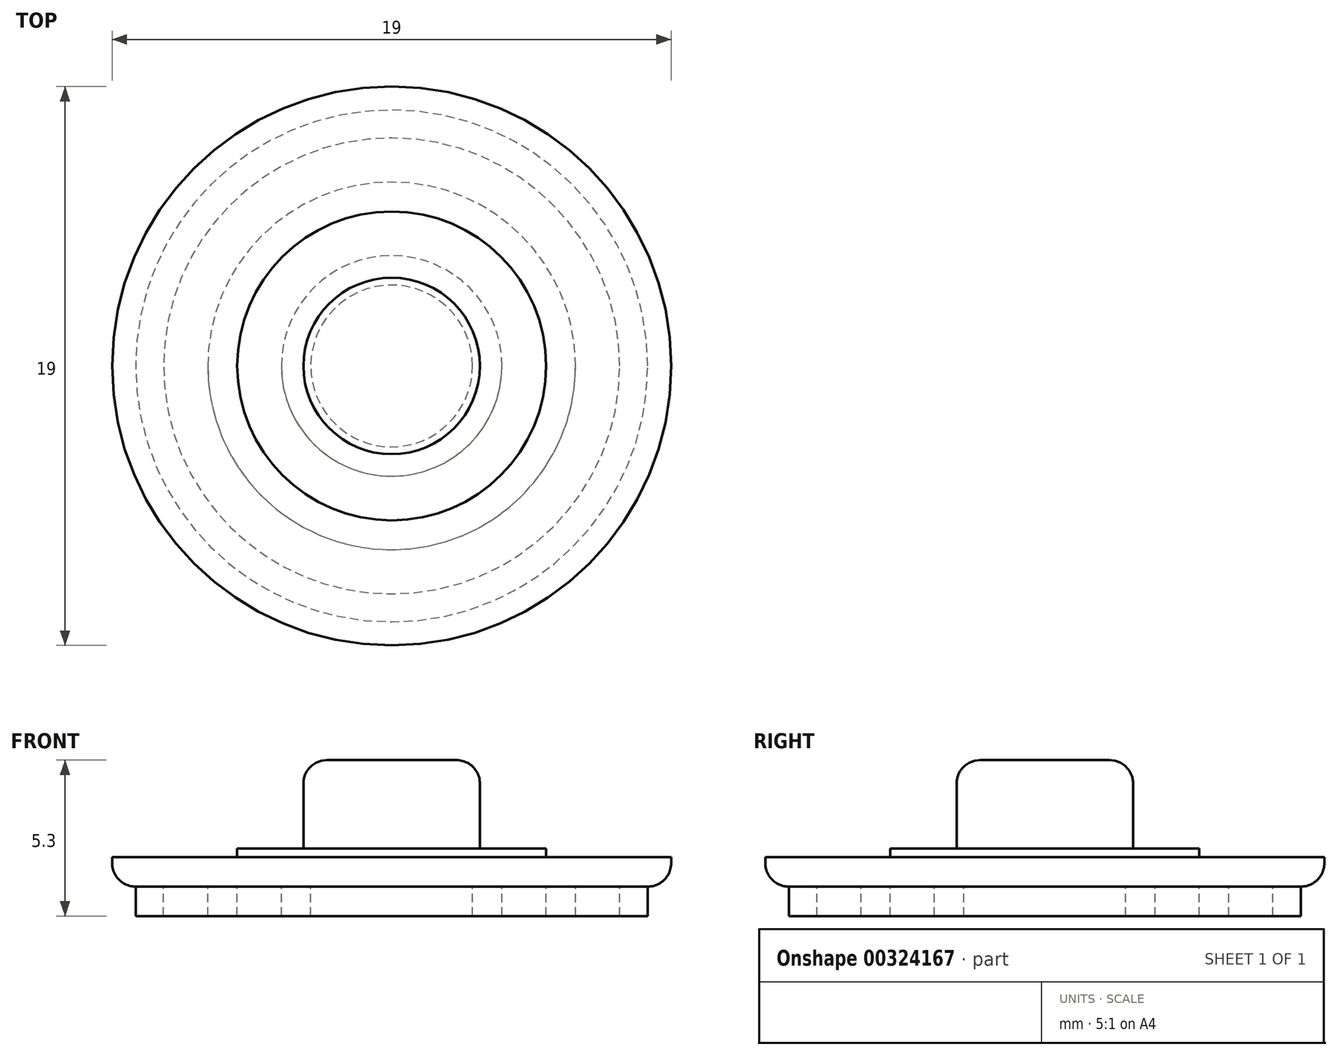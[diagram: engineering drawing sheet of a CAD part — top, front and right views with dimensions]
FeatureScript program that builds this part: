
annotation { "Feature Type Name" : "Feature", "Feature Type Description" : "" }
export const myFeature = defineFeature(function(context is Context, id is Id, definition is map)
    precondition{}
    {
        {
            var Q0;
            Q0=qCreatedBy(makeId("Top.planeOp"),FACE);
            var sketch = newSketch(context, id + "F0", { "sketchPlane" : qUnion([Q0])});
            skCircle(sketch, "E0", {"center": v(0, 0) * mm, "radius": 9.5 * mm});
            skSolve(sketch);
        }
        {
            var Q0;
            Q0=qSketchRegion(id+"F0",true);
            extrude(context, id + "F1", {"entities" : qUnion([Q0]), "depth" : 1 * mm});
        }
        {
            var Q0;
            Q0=makeQuery(id+"F1.opExtrude","CAP_FACE",FACE,{"disambiguationData":[OSD([sQuery(id+"F0.wireOp",EDGE,"E0")])],"isStart":false});
            var sketch = newSketch(context, id + "F2", { "sketchPlane" : qUnion([Q0])});
            skCircle(sketch, "E1", {"center": v(0, 0) * mm, "radius": 3 * mm});
            skSolve(sketch);
        }
        {
            var Q0;
            Q0=makeQuery(id+"F2.imprint","IMPRINT",FACE,{"disambiguationData":[TD([[makeQuery(id+"F2.imprint","IMPRINT",EDGE,{"derivedFrom":sQuery(id+"F2.wireOp",EDGE,"E1")}),1.0]])]});
            extrude(context, id + "F3", {"entities" : qUnion([Q0]), "operationType" : NewBodyOperationType.ADD, "depth" : 3.3 * mm});
        }
        {
            var Q0;
            Q0=makeQuery(id+"F1.opExtrude","CAP_EDGE",EDGE,{"disambiguationData":[OSD([sQuery(id+"F0.wireOp",EDGE,"E0")])],"isStart":true});
            var Q1;
            Q1=makeQuery(id+"F3.opExtrude","CAP_EDGE",EDGE,{"disambiguationData":[OSD([sQuery(id+"F2.wireOp",EDGE,"E1")])],"isStart":false});
            fillet(context, id + "F4", {"entities" : qUnion([Q0, Q1]), "radius" : .8 * mm, "tangentPropagation" : true, "allowEdgeOverflow" : false});
        }
        {
            var Q0;
            Q0=makeQuery(id+"F1.opExtrude","CAP_FACE",FACE,{"disambiguationData":[OSD([sQuery(id+"F0.wireOp",EDGE,"E0")])],"isStart":false});
            var sketch = newSketch(context, id + "F5", { "sketchPlane" : qUnion([Q0])});
            skCircle(sketch, "E2", {"center": v(0, 0) * mm, "radius": 5.25 * mm});
            skSolve(sketch);
        }
        {
            var Q0;
            Q0=makeQuery(id+"F5.imprint","IMPRINT",FACE,{"disambiguationData":[TD([[makeQuery(id+"F5.imprint","IMPRINT",EDGE,{"derivedFrom":makeQuery(id+"F3.opExtrude","CAP_EDGE",EDGE,{"disambiguationData":[OSD([sQuery(id+"F2.wireOp",EDGE,"E1")])],"isStart":true})}),1.0]])]});
            var Q1;
            Q1=makeQuery(id+"F5.imprint","IMPRINT",FACE,{"disambiguationData":[TD([[makeQuery(id+"F5.imprint","IMPRINT",EDGE,{"derivedFrom":sQuery(id+"F5.wireOp",EDGE,"E2")}),1.0]])]});
            extrude(context, id + "F6", {"entities" : qUnion([Q0, Q1]), "operationType" : NewBodyOperationType.ADD, "depth" : .3 * mm});
        }
        {
            var Q0;
            Q0=makeQuery(id+"F1.opExtrude","CAP_FACE",FACE,{"disambiguationData":[OSD([sQuery(id+"F0.wireOp",EDGE,"E0")])],"isStart":true});
            var sketch = newSketch(context, id + "F7", { "sketchPlane" : qUnion([Q0])});
            skCircle(sketch, "E3", {"center": v(0, 0) * mm, "radius": 8.75 * mm});
            skCircle(sketch, "E4", {"center": v(0, 0) * mm, "radius": 7.75 * mm});
            skCircle(sketch, "E5", {"center": v(0, 0) * mm, "radius": 6.25 * mm});
            skCircle(sketch, "E6", {"center": v(0, 0) * mm, "radius": 5.25 * mm});
            skCircle(sketch, "E7", {"center": v(0, 0) * mm, "radius": 3.75 * mm});
            skCircle(sketch, "E8", {"center": v(0, 0) * mm, "radius": 2.75 * mm});
            skSolve(sketch);
        }
        {
            var Q0;
            Q0=makeQuery(id+"F7.imprint","IMPRINT",FACE,{"disambiguationData":[TD([[makeQuery(id+"F7.imprint","IMPRINT",EDGE,{"derivedFrom":sQuery(id+"F7.wireOp",EDGE,"R4SnE7ev-gE2s-1cBr-oGM4-FRtO0DUmkkXN")}),1.0]])]});
            var Q1;
            Q1=makeQuery(id+"F7.imprint","IMPRINT",FACE,{"disambiguationData":[TD([[makeQuery(id+"F7.imprint","IMPRINT",EDGE,{"derivedFrom":sQuery(id+"F7.wireOp",EDGE,"E4")}),-1.0]])]});
            var Q2;
            Q2=makeQuery(id+"F7.imprint","IMPRINT",FACE,{"disambiguationData":[TD([[makeQuery(id+"F7.imprint","IMPRINT",EDGE,{"derivedFrom":sQuery(id+"F7.wireOp",EDGE,"E5")}),1.0]])]});
            var Q3;
            Q3=makeQuery(id+"F7.imprint","IMPRINT",FACE,{"disambiguationData":[TD([[makeQuery(id+"F7.imprint","IMPRINT",EDGE,{"derivedFrom":sQuery(id+"F7.wireOp",EDGE,"E7")}),1.0]])]});
            extrude(context, id + "F8", {"entities" : qUnion([Q0, Q1, Q2, Q3]), "operationType" : NewBodyOperationType.ADD, "depth" : 1 * mm});
        }
    });
